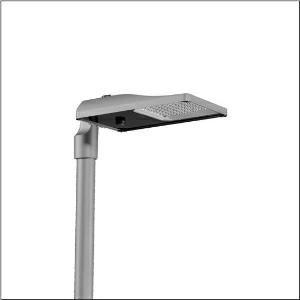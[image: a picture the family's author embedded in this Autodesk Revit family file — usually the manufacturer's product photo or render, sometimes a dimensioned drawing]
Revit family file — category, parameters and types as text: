
# Revit family: streetlight_sl_31_midi___st0_5a_5xh7b31t08la_752d
name_source: partatom
category: Lighting Fixtures
units: mm (PartAtom-declared; Revit-internal decimal feet)

## family parameters
Cut with Voids When Loaded = No
Host = Face
Light Source = No
Part Type = Normal
Room Calculation Point = No
Round Connector Dimension = Use Diameter
Shared = No

## types (1)
- --- (1 x LED, 13170 lm, 86.5 W, 3000K)
    Apparent Load = 87 VA
    CIE Flux Codes = 41 75 97 100 100
    Color Rendering = 70
    Color Temperature = 3000K
    Default Elevation = 1800 mm
    Description = Streetlight SL 31 midi, mast luminaire, primary light control with lens, of PMMA, primary optical cover: cover, of toughened safety glass, transparent, light distribution: ST0.5a, light emission: direct distribution, primary light characteristic: asymmetric, installation type: post-top, side-entry, LED, High Power LED, rated luminous flux: 13.170lm, luminous efficacy: 152lm/W, light colour: 730, colour temperature: 3000K, control: presetting dimming logarithmic, flexible luminous flux parameterisation, time-dependent luminous flux control, constant luminous flux control, power reduction, intelligent temperature release in ECG and LED module, overheat protection, with cable H07RN-F 2x 1.5mm², mains connection: 220..240V, AC, 50/60Hz, connection cable pre-assembled, cable length: 10,5m, start of lifetime: 87W, end of service life: 90W, reduction: 40W, luminaire housing, of diecast aluminium, powder-coated, Siteco® metallic grey (DB 702S), corrosivity category C5 high according to DIN EN ISO 12944, sealing non-destructively replaceable, multi-level sealing system, mast flange (76/60mm) included as standard, inclination: -15°..+20° (post-top) | -20°..+20° (side-entry), adjustable in 5° steps, no sealing on luminaire upper side, Smart Interface below and above, protection rating (complete): IP66, insulation class (complete): insulation class II (safety insulation), certification: CE, ENEC, ENEC+, VDE, UKCA, ZD4i, impact resistance: IK09, permissible operating ambient temperature for outdoor applications: -40..+50°C, standard-compliant lighting for roads and squares, packaging unit: 1 piece

Light Distribution: ST0.5a
    Height = 79 mm
    Lamp = 1 x LED
    Lamp Light Flux = 13170 lm
    Lamp Power = 86.5 W
    Lamp count = 1
    Length = 577 mm
    Luminous efficacy = 152 lm/W
    Manufacturer = Siteco
    ModVariant = No
    Model = 5XH7B31T08LA
    Number of Poles = 1
    OnlyDefault = Yes
    Power Factor = 1
    Product Name = Streetlight SL 31 midi | ST0.5a
    Product group = mast luminaire | pylon top
    ProductGroupID = 6100
    Protection Class = Protection class II
    Protection Degree = IP 66
    RLX_Detail_Level = 1
    RLX_Emergency_Light_Flux = 0 lm
    RLX_Emergency_Type = 0
    RLX_Emergency_Type_DB = No
    RlxData = <blob elided: 54097 chars, md5=530e18e4>
    Socket = socket
    Standby Power = 0 W
    System Light Flux = 13170 lm
    System Power = 87 W
    Type Comments = factory setting: luminous flux: 100 % | dim-lin: 254 | 456 mA
    Type Image = l_1300321.jpg
    URL = http://relux.com
    VarID = @adj_016431
    Voltage = 0 V
    Weight = 0.00 kg
    Width = 362 mm

## geometry (parser evidence)
native form markers: Blend x4, Sweep x11
no freeform markers — native parametric forms only
